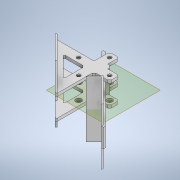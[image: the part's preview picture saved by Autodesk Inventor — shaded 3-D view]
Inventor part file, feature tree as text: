
AUTODESK INVENTOR PART (.ipt)
format: ipt  version: 2020 (Build 240168000, 168)  size: 503,296 bytes
history: native  units: mm
features: extrude x10, sketch x10, chamfer x6, mirror x5, plane x1
ambient origin geometry x8: Origin, YZ Plane, XZ Plane, XY Plane, X Axis, Y Axis, Z Axis, Center Point
bodies: Solid1 (feature_tree)
feature tree (32):
  extrude  "Extrusion1"  Depth=4.0mm
  chamfer  "Chamfer1"  Distance=3.0mm
  extrude  "Extrusion2"  Depth=5.0mm
  plane  "Work Plane1"
  mirror  "Mirror1"
  chamfer  "Chamfer2"  Distance=5.0mm
  extrude  "Extrusion3"  Depth=5.0mm
  chamfer  "Chamfer3"  Distance=5.0mm
  extrude  "Extrusion4"  Depth=3.0mm TaperAngle=0.0deg
  chamfer  "Chamfer4"  Distance=2.0mm Angle=45.0deg
  extrude  "Extrusion5"  TaperAngle=0.0deg  [1 undecoded]
  extrude  "Extrusion6"  Depth=3.0mm
  extrude  "Extrusion7"  Depth=25.0mm
  mirror  "Mirror5"
  mirror  "Mirror6"
  chamfer  "Chamfer5"  Distance=75.0mm
  extrude  "Extrusion8"  Depth=10.0mm TaperAngle=0.0deg
  chamfer  "Chamfer6"  Distance=1.5mm Angle=45.0deg
  extrude  "Extrusion9"  Depth=5.0mm
  mirror  "Mirror7"
  mirror  "Mirror8"
  extrude  "Extrusion10"  Depth=5.0mm
  sketch  "Sketch1"  dims[d0=4.0mm d1=4.0mm]
  sketch  "Sketch3"  dims[d2=16.5mm]
  sketch  "Sketch4"  dims[d3=16.5mm]
  sketch  "Sketch5"  dims[d4=4.0mm]
  sketch  "Sketch6"  dims[d5=4.0mm]
  sketch  "Sketch7"  dims[d6=16.5mm]
  sketch  "Sketch8"  dims[d7=16.5mm]
  sketch  "Sketch9"  dims[d8=3.0mm]
  sketch  "Sketch10"  dims[d9=10.0mm]
  sketch  "Sketch11"  dims[d10=3.0mm d11=3.0mm d12=5.0mm d13=5.0mm d14=5.0mm d15=5.0mm d16=3.0mm d17=0.0mm d18=2.0mm d19=2.0mm d20=45.0deg d25=0.0mm d26=3.0mm d27=25.0mm d28=75.0mm d29=10.0mm d30=0.0mm d31=0.0mm d32=1.5mm d33=2.0mm d34=45.0deg d35=5.0mm d36=5.0mm d37=3.0mm d38=0.0mm d39=3.0mm d40=2.0mm d41=45.0deg d42=6.0mm d43=6.0mm d44=3.0mm d45=0.0mm d46=2.0mm d47=2.0mm d48=45.0deg d50=6.0mm d51=6.0mm d52=2.0mm d53=0.0mm d54=6.0mm d55=6.0mm d56=18.0mm d57=0.0mm d58=45.0deg d59=45.0deg d60=3.0mm d61=3.0mm d62=6.0mm d63=6.0mm d64=2.0mm d65=0.0mm d66=2.0mm d67=2.0mm d68=45.0deg d69=36.0mm d70=11.5mm d71=1.5mm d72=60.0mm d73=0.0mm d74=1.5mm d75=2.0mm d76=45.0deg d80=3.0mm d81=3.0mm d82=15.0mm d83=15.0mm d87=22.68928mm d88=3.0mm d89=6.0mm d90=10.0mm d91=6.0mm d92=0.0mm d93=0.0mm d94=18.0mm d95=3.0mm d96=0.0mm d97=3.0mm d98=3.0mm d101=22.274mm d102=22.274mm d103=1.414mm d104=0.0mm]
note: 1 required parameter value undecoded (feature->parameter linkage not recoverable at this tier; creation-order binding heuristic only, values carry confidence <= 0.55)
